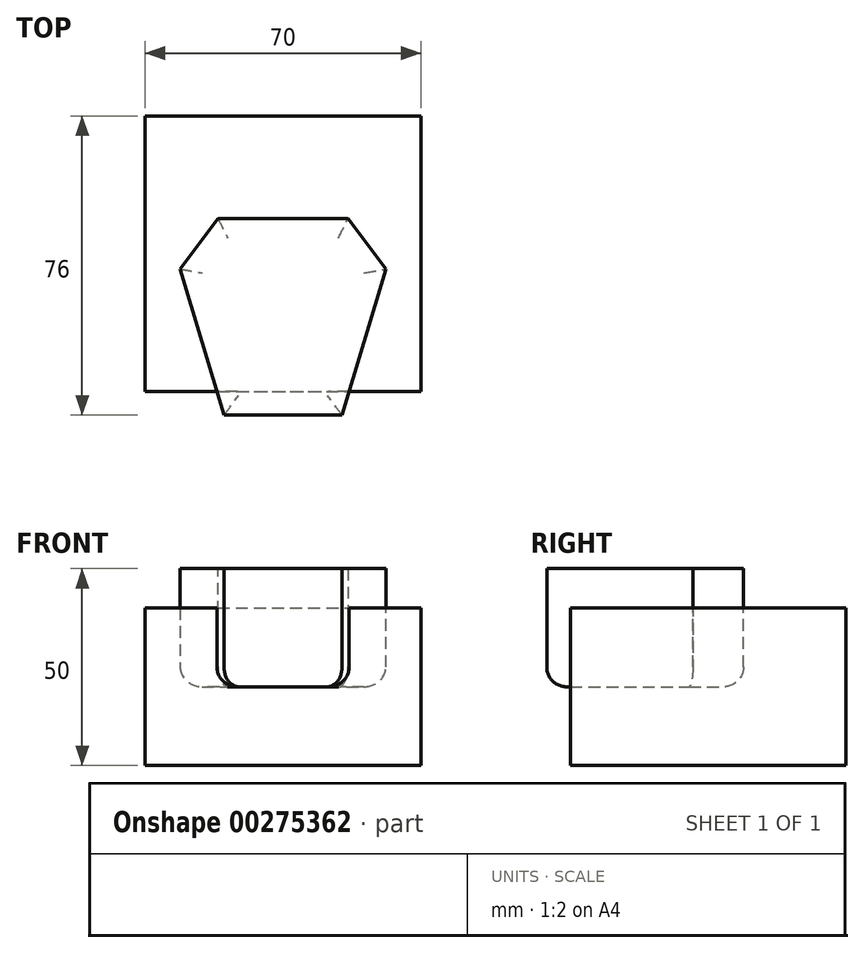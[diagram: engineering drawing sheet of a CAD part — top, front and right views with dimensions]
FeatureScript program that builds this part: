
annotation { "Feature Type Name" : "Feature", "Feature Type Description" : "" }
export const myFeature = defineFeature(function(context is Context, id is Id, definition is map)
    precondition{}
    {
        {
            var Q0;
            Q0=qCreatedBy(makeId("Top.planeOp"),FACE);
            var sketch = newSketch(context, id + "F0", { "sketchPlane" : qUnion([Q0])});
            skLineSegment(sketch, "E0", {"start": v(0, 100.57) * mm, "end": v(0, -68.31) * mm, "construction": true});
            skLineSegment(sketch, "E1", {"start": v(0, 0) * mm, "end": v(-15, 0) * mm});
            skLineSegment(sketch, "E2", {"start": v(-15, 0) * mm, "end": v(-30, 50) * mm});
            skLineSegment(sketch, "E3", {"start": v(-30, 50) * mm, "end": v(0, 50) * mm});
            skLineSegment(sketch, "E4.MirrorCS", {"start": v(30, 50) * mm, "end": v(0, 50) * mm});
            skLineSegment(sketch, "E5.MirrorCS", {"start": v(15, 0) * mm, "end": v(30, 50) * mm});
            skLineSegment(sketch, "E6.MirrorCS", {"start": v(0, 0) * mm, "end": v(15, 0) * mm});
            skSolve(sketch);
        }
        {
            var Q0;
            Q0=qSketchRegion(id+"F0",true);
            extrude(context, id + "F1", {"entities" : qUnion([Q0]), "depth" : 30 * mm});
        }
        {
            var Q0;
            Q0=makeQuery(id+"F1.opExtrude","SWEPT_EDGE",EDGE,{"disambiguationData":[OSD([sQuery(id+"F0.wireOp",EDGE,"E2"),sQuery(id+"F0.wireOp",EDGE,"E3")])]});
            var Q1;
            Q1=makeQuery(id+"F1.opExtrude","SWEPT_EDGE",EDGE,{"disambiguationData":[OSD([sQuery(id+"F0.wireOp",EDGE,"E4.MirrorCS"),sQuery(id+"F0.wireOp",EDGE,"E5.MirrorCS")])]});
            chamfer(context, id + "F2", {"entities" : qUnion([Q0, Q1]), "width" : 10 * mm, "tangentPropagation" : true});
        }
        {
            var Q0;
            Q0=makeQuery(id+"F1.opExtrude","CAP_FACE",FACE,{"disambiguationData":[OSD([sQuery(id+"F0.wireOp",EDGE,"E1"),sQuery(id+"F0.wireOp",EDGE,"E2"),sQuery(id+"F0.wireOp",EDGE,"E3"),sQuery(id+"F0.wireOp",EDGE,"E4.MirrorCS"),sQuery(id+"F0.wireOp",EDGE,"E5.MirrorCS"),sQuery(id+"F0.wireOp",EDGE,"E6.MirrorCS")])],"isStart":true});
            fillet(context, id + "F3", {"entities" : qUnion([Q0]), "radius" : 5 * mm, "tangentPropagation" : true, "allowEdgeOverflow" : false});
        }
        {
            var Q0;
            Q0=qCreatedBy(makeId("Top.planeOp"),FACE);
            var sketch = newSketch(context, id + "F4", { "sketchPlane" : qUnion([Q0])});
            skLineSegment(sketch, "E7.bottom", {"start": v(-35, 6) * mm, "end": v(35, 6) * mm});
            skLineSegment(sketch, "E7.top", {"start": v(-35, 76) * mm, "end": v(35, 76) * mm});
            skLineSegment(sketch, "E7.left", {"start": v(-35, 6) * mm, "end": v(-35, 76) * mm});
            skLineSegment(sketch, "E7.right", {"start": v(35, 6) * mm, "end": v(35, 76) * mm});
            skLineSegment(sketch, "E8", {"start": v(0, 114.32) * mm, "end": v(0, -45.79) * mm, "construction": true});
            skPoint(sketch, "E9", {"position": v(0, 6) * mm});
            skSolve(sketch);
        }
        {
            var Q0;
            Q0=qSketchRegion(id+"F4",true);
            extrude(context, id + "F5", {"entities" : qUnion([Q0]), "depth" : 20 * mm, "hasSecondDirection" : true, "secondDirectionOppositeDirection" : true, "secondDirectionDepth" : 20 * mm});
        }
        {
            var Q0;
            Q0=makeQuery(id+"F1.opExtrude","SWEPT_BODY",BODY,{"disambiguationData":[OSD([sQuery(id+"F0.wireOp",EDGE,"E1"),sQuery(id+"F0.wireOp",EDGE,"E2"),sQuery(id+"F0.wireOp",EDGE,"E3"),sQuery(id+"F0.wireOp",EDGE,"E4.MirrorCS"),sQuery(id+"F0.wireOp",EDGE,"E5.MirrorCS"),sQuery(id+"F0.wireOp",EDGE,"E6.MirrorCS")])]});
            var Q1;
            Q1=makeQuery(id+"F5.opExtrude","SWEPT_BODY",BODY,{"disambiguationData":[OSD([sQuery(id+"F4.wireOp",EDGE,"E7.bottom"),sQuery(id+"F4.wireOp",EDGE,"E7.top"),sQuery(id+"F4.wireOp",EDGE,"E7.left"),sQuery(id+"F4.wireOp",EDGE,"E7.right")])]});
            var Q2;
            Q2=makeQuery(id+"F1.opExtrude","SWEPT_FACE",FACE,{"disambiguationData":[OSD([sQuery(id+"F0.wireOp",EDGE,"E5.MirrorCS")])]});
            var Q3;
            Q3=makeQuery(id+"F2.opChamfer","BLEND_FACE",FACE,{"disambiguationData":[OSD([sQuery(id+"F0.wireOp",EDGE,"E4.MirrorCS"),sQuery(id+"F0.wireOp",EDGE,"E5.MirrorCS")])]});
            var Q4;
            Q4=makeQuery(id+"F1.opExtrude","SWEPT_FACE",FACE,{"disambiguationData":[OSD([sQuery(id+"F0.wireOp",EDGE,"E3"),sQuery(id+"F0.wireOp",EDGE,"E4.MirrorCS")])]});
            var Q5;
            Q5=makeQuery(id+"F2.opChamfer","BLEND_FACE",FACE,{"disambiguationData":[OSD([sQuery(id+"F0.wireOp",EDGE,"E2"),sQuery(id+"F0.wireOp",EDGE,"E3")])]});
            var Q6;
            Q6=makeQuery(id+"F1.opExtrude","SWEPT_FACE",FACE,{"disambiguationData":[OSD([sQuery(id+"F0.wireOp",EDGE,"E2")])]});
            booleanBodies(context, id + "F6", {"operationType" : BooleanOperationType.SUBTRACTION, "tools" : qUnion([Q0]), "targets" : qUnion([Q1]), "entitiesToOffset" : qUnion([Q2, Q3, Q4, Q5, Q6]), "keepTools" : true});
        }
    });
